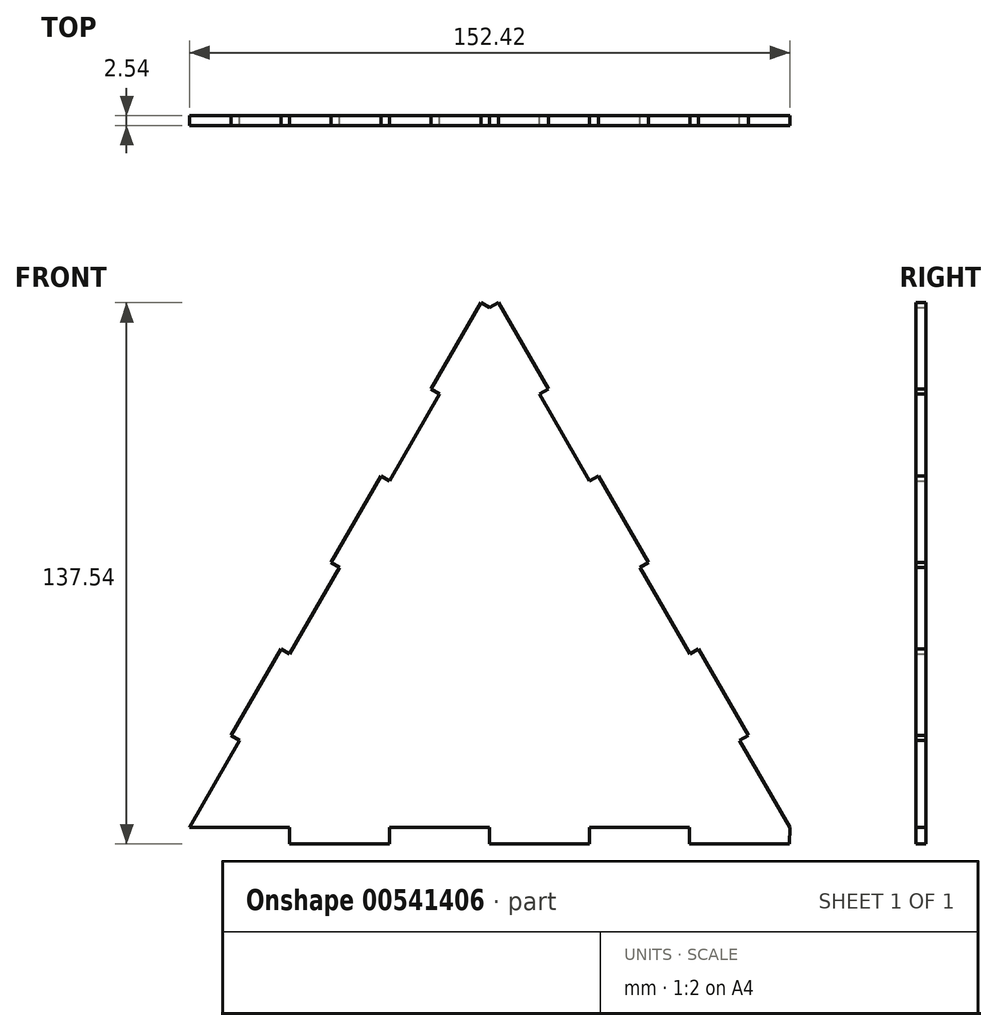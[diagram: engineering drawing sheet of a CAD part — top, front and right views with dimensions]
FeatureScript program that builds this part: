
annotation { "Feature Type Name" : "Feature", "Feature Type Description" : "" }
export const myFeature = defineFeature(function(context is Context, id is Id, definition is map)
    precondition{}
    {
        {
            var Q0;
            Q0=qCreatedBy(makeId("Front.planeOp"),FACE);
            var sketch = newSketch(context, id + "F0", { "sketchPlane" : qUnion([Q0])});
            skLineSegment(sketch, "E0", {"start": v(0, 62.62) * mm, "end": v(-76.21, -69.38) * mm});
            skLineSegment(sketch, "E1", {"start": v(-76.21, -69.38) * mm, "end": v(76.21, -69.38) * mm});
            skLineSegment(sketch, "E2", {"start": v(76.21, -69.38) * mm, "end": v(0, 62.62) * mm});
            skLineSegment(sketch, "E3", {"start": v(0, 62.62) * mm, "end": v(-2.2, 63.9) * mm});
            skLineSegment(sketch, "E4", {"start": v(-2.2, 63.9) * mm, "end": v(-14.9, 41.9) * mm});
            skLineSegment(sketch, "E5", {"start": v(-14.9, 41.9) * mm, "end": v(-12.7, 40.63) * mm});
            skLineSegment(sketch, "E6", {"start": v(-12.7, 40.63) * mm, "end": v(-25.4, 18.63) * mm});
            skLineSegment(sketch, "E7", {"start": v(-25.4, 18.63) * mm, "end": v(-27.6, 19.9) * mm});
            skLineSegment(sketch, "E8", {"start": v(-27.6, 19.9) * mm, "end": v(-40.3, -2.1) * mm});
            skLineSegment(sketch, "E9", {"start": v(-40.3, -2.1) * mm, "end": v(-38.1, -3.37) * mm});
            skLineSegment(sketch, "E10", {"start": v(-38.1, -3.37) * mm, "end": v(-50.8, -25.36) * mm});
            skLineSegment(sketch, "E11", {"start": v(-50.8, -25.36) * mm, "end": v(-53, -24.1) * mm});
            skLineSegment(sketch, "E12", {"start": v(-53, -24.1) * mm, "end": v(-65.7, -46.1) * mm});
            skLineSegment(sketch, "E13", {"start": v(-65.7, -46.1) * mm, "end": v(-63.5, -47.36) * mm});
            skLineSegment(sketch, "E14", {"start": v(-76.21, -69.38) * mm, "end": v(-50.81, -69.38) * mm});
            skLineSegment(sketch, "E15", {"start": v(-50.81, -69.38) * mm, "end": v(-50.81, -73.65) * mm});
            skLineSegment(sketch, "E16", {"start": v(-50.81, -73.65) * mm, "end": v(-25.41, -73.65) * mm});
            skLineSegment(sketch, "E17", {"start": v(-25.41, -73.65) * mm, "end": v(-25.41, -69.38) * mm});
            skLineSegment(sketch, "E18", {"start": v(-25.41, -69.38) * mm, "end": v(0, -69.38) * mm});
            skLineSegment(sketch, "E19", {"start": v(0, -69.38) * mm, "end": v(0, -73.65) * mm});
            skLineSegment(sketch, "E20", {"start": v(0, -73.65) * mm, "end": v(25.4, -73.65) * mm});
            skLineSegment(sketch, "E21", {"start": v(25.4, -73.65) * mm, "end": v(25.4, -69.38) * mm});
            skLineSegment(sketch, "E22", {"start": v(25.4, -69.38) * mm, "end": v(50.8, -69.38) * mm});
            skLineSegment(sketch, "E23", {"start": v(50.8, -69.38) * mm, "end": v(50.8, -73.65) * mm});
            skLineSegment(sketch, "E24", {"start": v(50.8, -73.65) * mm, "end": v(76.2, -73.65) * mm});
            skLineSegment(sketch, "E25", {"start": v(76.2, -73.65) * mm, "end": v(76.21, -69.38) * mm});
            skLineSegment(sketch, "E26", {"start": v(76.21, -69.38) * mm, "end": v(63.5, -47.37) * mm});
            skLineSegment(sketch, "E27", {"start": v(63.5, -47.37) * mm, "end": v(65.7, -46.1) * mm});
            skLineSegment(sketch, "E28", {"start": v(65.7, -46.1) * mm, "end": v(53, -24.1) * mm});
            skLineSegment(sketch, "E29", {"start": v(53, -24.1) * mm, "end": v(50.8, -25.37) * mm});
            skLineSegment(sketch, "E30", {"start": v(50.8, -25.37) * mm, "end": v(38.1, -3.38) * mm});
            skLineSegment(sketch, "E31", {"start": v(38.1, -3.38) * mm, "end": v(40.3, -2.1) * mm});
            skLineSegment(sketch, "E32", {"start": v(40.3, -2.1) * mm, "end": v(27.6, 19.9) * mm});
            skLineSegment(sketch, "E33", {"start": v(27.6, 19.9) * mm, "end": v(25.4, 18.63) * mm});
            skLineSegment(sketch, "E34", {"start": v(25.4, 18.63) * mm, "end": v(12.7, 40.63) * mm});
            skLineSegment(sketch, "E35", {"start": v(12.7, 40.63) * mm, "end": v(14.9, 41.9) * mm});
            skLineSegment(sketch, "E36", {"start": v(0, 62.62) * mm, "end": v(2.2, 63.9) * mm});
            skLineSegment(sketch, "E37", {"start": v(2.2, 63.9) * mm, "end": v(14.9, 41.9) * mm});
            skSolve(sketch);
        }
        {
            var Q0;
            Q0=qSketchRegion(id+"F0",true);
            extrude(context, id + "F1", {"entities" : qUnion([Q0]), "depth" : 2.54 * mm, "offsetDistance" : 25.4 * mm});
        }
    });
